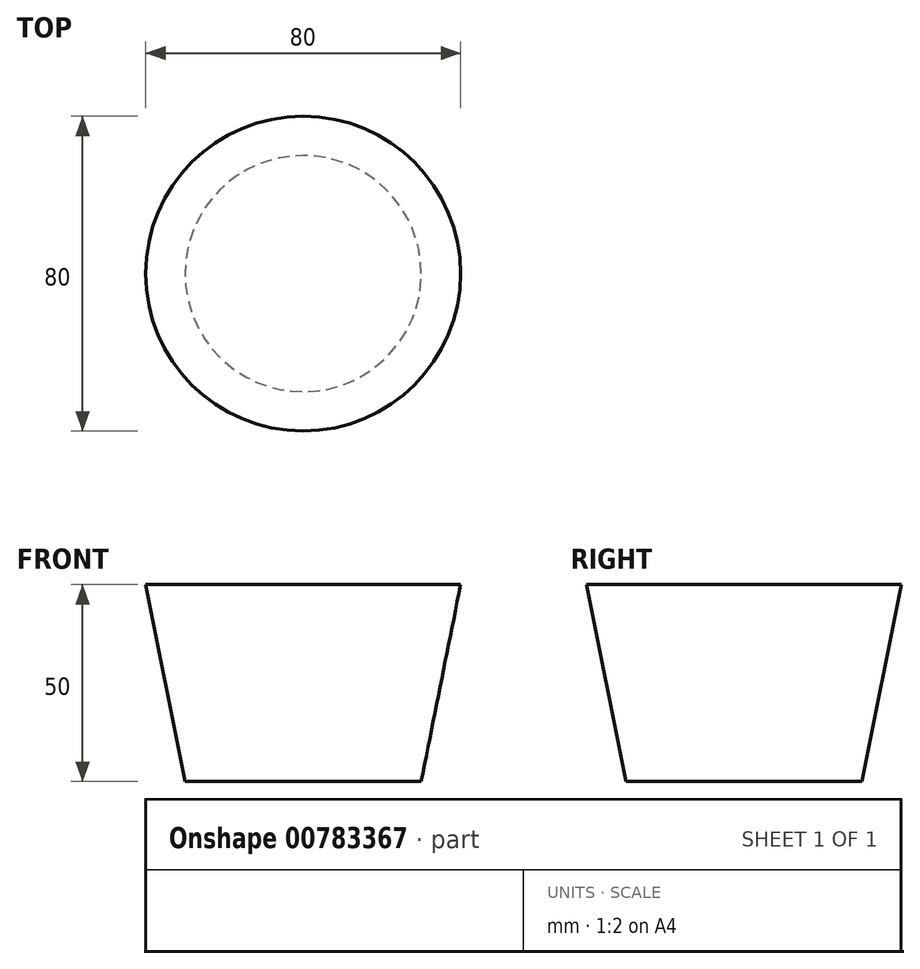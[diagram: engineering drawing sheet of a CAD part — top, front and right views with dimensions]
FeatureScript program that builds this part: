
annotation { "Feature Type Name" : "Feature", "Feature Type Description" : "" }
export const myFeature = defineFeature(function(context is Context, id is Id, definition is map)
    precondition{}
    {
        {
            var Q0;
            Q0=qCreatedBy(makeId("Top.planeOp"),FACE);
            cPlane(context, id + "F0", {"entities" : qUnion([Q0]), "cplaneType" : CPlaneType.OFFSET, "offset" : 25 * mm, "width" : 150 * mm, "height" : 150 * mm});
        }
        {
            var Q0;
            Q0=qCreatedBy(makeId("Top.planeOp"),FACE);
            cPlane(context, id + "F1", {"entities" : qUnion([Q0]), "cplaneType" : CPlaneType.OFFSET, "offset" : 25 * mm, "oppositeDirection" : true, "width" : 150 * mm, "height" : 150 * mm});
        }
        {
            var Q0;
            Q0=qCreatedBy(id+"F0.planeOp",FACE);
            var sketch = newSketch(context, id + "F2", { "sketchPlane" : qUnion([Q0])});
            skCircle(sketch, "E0", {"center": v(0, 0) * mm, "radius": 40 * mm});
            skSolve(sketch);
        }
        {
            var Q0;
            Q0=qCreatedBy(makeId("Top.planeOp"),FACE);
            var sketch = newSketch(context, id + "F3", { "sketchPlane" : qUnion([Q0])});
            skCircle(sketch, "E1", {"center": v(0, 0) * mm, "radius": 35 * mm});
            skSolve(sketch);
        }
        {
            var Q0;
            Q0=qCreatedBy(id+"F1.planeOp",FACE);
            var sketch = newSketch(context, id + "F4", { "sketchPlane" : qUnion([Q0])});
            skCircle(sketch, "E2", {"center": v(0, 0) * mm, "radius": 30 * mm});
            skSolve(sketch);
        }
        {
            var Q0;
            Q0 = qSketchRegion(id + "F2", true);
            var Q1;
            Q1 = qSketchRegion(id + "F3", true);
            var Q2;
            Q2 = qSketchRegion(id + "F4", true);
            loft(context, id + "F5", {"sheetProfilesArray" : [{ "sheetProfileEntities" : qUnion([Q0]) }, { "sheetProfileEntities" : qUnion([Q1]) }, { "sheetProfileEntities" : qUnion([Q2]) }]});
        }
    });
